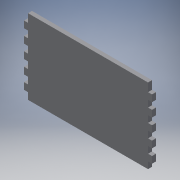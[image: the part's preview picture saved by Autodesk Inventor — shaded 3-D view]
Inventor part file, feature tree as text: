
AUTODESK INVENTOR PART (.ipt)
format: ipt  version: 2019 (Build 230136000, 136)  size: 133,632 bytes
history: native  units: mm
features: reference x14, other x5, extrude x1, sketch x1
ambient origin geometry x8: Origin, YZ Plane, XZ Plane, XY Plane, X Axis, Y Axis, Z Axis, Center Point
bodies: Body1 (feature_tree)
feature tree (21):
  other  "Твердое тело1"
  extrude  "Выдавливание1"  Depth=6.0mm TaperAngle=0.0deg
  sketch  "Эскиз1"
  reference  "Ссылка1"
  reference  "Ссылка2"
  reference  "Ссылка3"
  reference  "Ссылка4"
  reference  "Ссылка5"
  reference  "Ссылка6"
  reference  "Ссылка7"
  reference  "Ссылка8"
  reference  "Ссылка9"
  reference  "Ссылка10"
  reference  "Ссылка11"
  reference  "Ссылка12"
  reference  "Ссылка13"
  reference  "Ссылка14"
  other  "<userpath>\Desktop\Новая папка (7)\Сборка2.iam"
  other  "Сборка2.iam"
  other  "боковина:2"
  other  "боковина:1"
